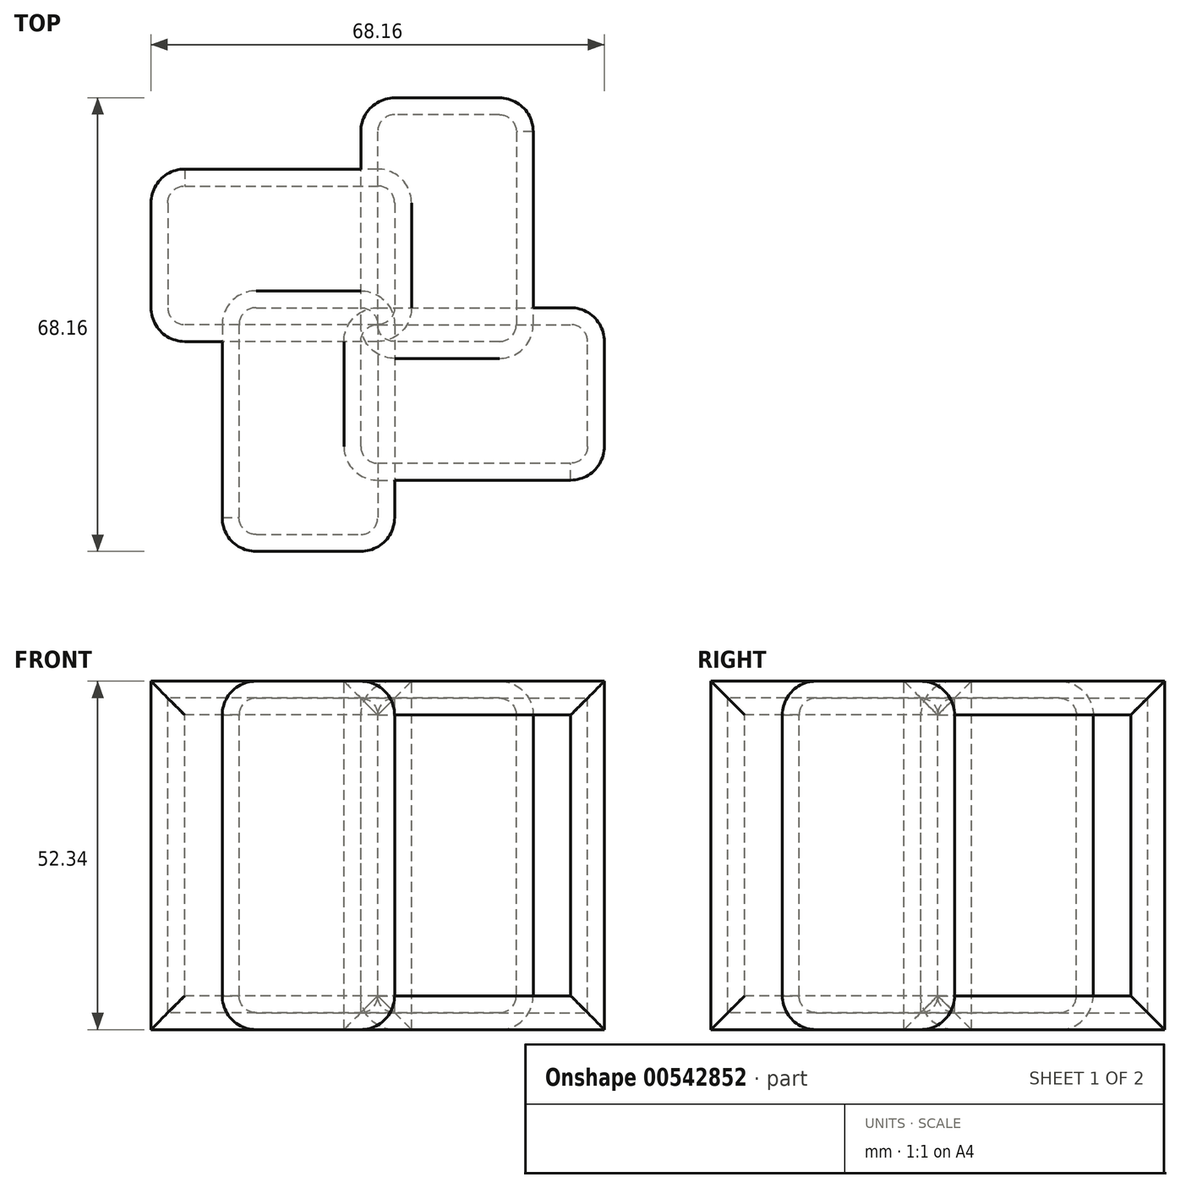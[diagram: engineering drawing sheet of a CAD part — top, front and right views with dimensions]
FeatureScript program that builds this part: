
annotation { "Feature Type Name" : "Feature", "Feature Type Description" : "" }
export const myFeature = defineFeature(function(context is Context, id is Id, definition is map)
    precondition{}
    {
        {
            var Q0;
            Q0=qCreatedBy(makeId("Front.planeOp"),FACE);
            var sketch = newSketch(context, id + "F0", { "sketchPlane" : qUnion([Q0])});
            skLineSegment(sketch, "E0.bottom", {"start": v(0, 0) * mm, "end": v(39.16, 0) * mm});
            skLineSegment(sketch, "E0.top", {"start": v(0, 52.34) * mm, "end": v(39.16, 52.34) * mm});
            skLineSegment(sketch, "E0.left", {"start": v(0, 0) * mm, "end": v(0, 52.34) * mm});
            skLineSegment(sketch, "E0.right", {"start": v(39.16, 0) * mm, "end": v(39.16, 52.34) * mm});
            skSolve(sketch);
        }
        {
            var Q0;
            Q0=makeQuery(id+"F0.imprint","IMPRINT",FACE,{"disambiguationData":[TD([[makeQuery(id+"F0.imprint","IMPRINT",EDGE,{"derivedFrom":sQuery(id+"F0.wireOp",EDGE,"E0.bottom")}),1.0]])]});
            extrude(context, id + "F1", {"entities" : qUnion([Q0]), "depth" : 25.9 * mm, "offsetDistance" : 25.4 * mm});
        }
        {
            var Q0;
            Q0=makeQuery(id+"F1.opExtrude","CAP_FACE",FACE,{"disambiguationData":[OSD([sQuery(id+"F0.wireOp",EDGE,"E0.bottom"),sQuery(id+"F0.wireOp",EDGE,"E0.top"),sQuery(id+"F0.wireOp",EDGE,"E0.left"),sQuery(id+"F0.wireOp",EDGE,"E0.right")])],"isStart":true});
            fillet(context, id + "F2", {"entities" : qUnion([Q0]), "radius" : 5.08 * mm, "tangentPropagation" : true, "allowEdgeOverflow" : false});
        }
        {
            var Q0;
            Q0=makeQuery(id+"F1.opExtrude","CAP_FACE",FACE,{"disambiguationData":[OSD([sQuery(id+"F0.wireOp",EDGE,"E0.bottom"),sQuery(id+"F0.wireOp",EDGE,"E0.top"),sQuery(id+"F0.wireOp",EDGE,"E0.left"),sQuery(id+"F0.wireOp",EDGE,"E0.right")])],"isStart":false});
            fillet(context, id + "F3", {"entities" : qUnion([Q0]), "radius" : 5.08 * mm, "tangentPropagation" : true, "allowEdgeOverflow" : false});
        }
        {
            var Q0;
            Q0=makeQuery(id+"F1.opExtrude","CAP_FACE",FACE,{"disambiguationData":[OSD([sQuery(id+"F0.wireOp",EDGE,"E0.bottom"),sQuery(id+"F0.wireOp",EDGE,"E0.top"),sQuery(id+"F0.wireOp",EDGE,"E0.left"),sQuery(id+"F0.wireOp",EDGE,"E0.right")])],"isStart":false});
            shell(context, id + "F4", {"entities" : qUnion([Q0]), "thickness" : 2.54 * mm});
        }
        {
            var Q0;
            Q0=makeQuery(id+"F1.opExtrude","SWEPT_BODY",BODY,{"disambiguationData":[OSD([sQuery(id+"F0.wireOp",EDGE,"E0.bottom"),sQuery(id+"F0.wireOp",EDGE,"E0.top"),sQuery(id+"F0.wireOp",EDGE,"E0.left"),sQuery(id+"F0.wireOp",EDGE,"E0.right")])]});
            var Q1;
            {var subQ0=sQuery(id+"F0.wireOp",EDGE,"E0.right");var subQ1=sQuery(id+"F0.wireOp",EDGE,"E0.left");var subQ2=sQuery(id+"F0.wireOp",EDGE,"E0.top");var subQ3=sQuery(id+"F0.wireOp",EDGE,"E0.bottom");Q1=makeQuery(id+"F4.opShell","OFFSET_EDGE",EDGE,{"disambiguationData":[OSD([subQ3,subQ2,subQ1,subQ0]),TDD([makeQuery(id+"F2.opFillet","BLEND_EDGE",EDGE,{"blendedFrom":[makeQuery(id+"F1.opExtrude","CAP_EDGE",EDGE,{"disambiguationData":[OSD([subQ1])],"isStart":true}),makeQuery(id+"F1.opExtrude","CAP_FACE",FACE,{"disambiguationData":[OSD([subQ3,subQ2,subQ1,subQ0])],"isStart":true})],"blendedInto":[makeQuery(id+"F1.opExtrude","CAP_FACE",FACE,{"disambiguationData":[OSD([subQ3,subQ2,subQ1,subQ0])],"isStart":true})]})])]});}
            circularPattern(context, id + "F5", {"entities" : qUnion([Q0]), "axis" : qUnion([Q1]), "angle" : 360 * degree, "instanceCount" : 4, "equalSpace" : true});
        }
    });
